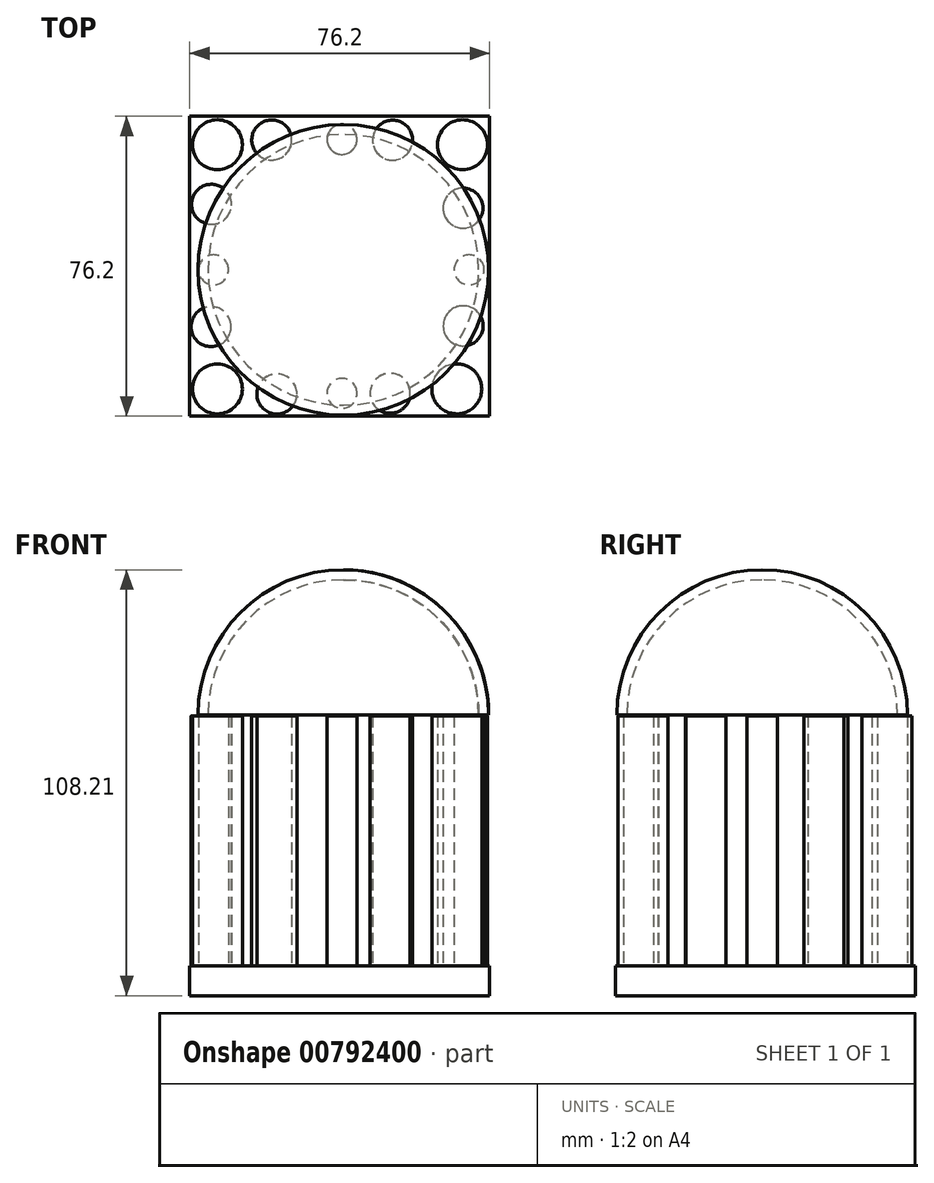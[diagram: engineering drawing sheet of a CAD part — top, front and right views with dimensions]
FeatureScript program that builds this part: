
annotation { "Feature Type Name" : "Feature", "Feature Type Description" : "" }
export const myFeature = defineFeature(function(context is Context, id is Id, definition is map)
    precondition{}
    {
        {
            var Q0;
            Q0=qCreatedBy(makeId("Top.planeOp"),FACE);
            var sketch = newSketch(context, id + "F0", { "sketchPlane" : qUnion([Q0])});
            skLineSegment(sketch, "E0.bottom", {"start": v(-38.66, 38.98) * mm, "end": v(37.54, 38.98) * mm});
            skLineSegment(sketch, "E0.top", {"start": v(-38.66, -37.22) * mm, "end": v(37.54, -37.22) * mm});
            skLineSegment(sketch, "E0.left", {"start": v(-38.66, 38.98) * mm, "end": v(-38.66, -37.22) * mm});
            skLineSegment(sketch, "E0.right", {"start": v(37.54, 38.98) * mm, "end": v(37.54, -37.22) * mm});
            skSolve(sketch);
        }
        {
            var Q0;
            Q0=makeQuery(id+"F0.imprint","IMPRINT",FACE,{"disambiguationData":[TD([[makeQuery(id+"F0.imprint","IMPRINT",EDGE,{"derivedFrom":sQuery(id+"F0.wireOp",EDGE,"E0.bottom")}),-1.0]])]});
            extrude(context, id + "F1", {"entities" : qUnion([Q0]), "depth" : 7.62 * mm, "offsetDistance" : 25.4 * mm});
        }
        {
            var Q0;
            Q0=makeQuery(id+"F1.opExtrude","CAP_FACE",FACE,{"disambiguationData":[OSD([sQuery(id+"F0.wireOp",EDGE,"E0.bottom"),sQuery(id+"F0.wireOp",EDGE,"E0.top"),sQuery(id+"F0.wireOp",EDGE,"E0.left"),sQuery(id+"F0.wireOp",EDGE,"E0.right")])],"isStart":false});
            var sketch = newSketch(context, id + "F2", { "sketchPlane" : qUnion([Q0])});
            skCircle(sketch, "E1", {"center": v(-31.66, -30.26) * mm, "radius": 6.35 * mm});
            skCircle(sketch, "E2", {"center": v(-31.66, 31.75) * mm, "radius": 6.35 * mm});
            skCircle(sketch, "E3", {"center": v(30.63, 31.75) * mm, "radius": 6.35 * mm});
            skCircle(sketch, "E4", {"center": v(29.17, -30.26) * mm, "radius": 6.35 * mm});
            skSolve(sketch);
        }
        {
            var Q0;
            Q0 = qSketchRegion(id + "F2", true);
            extrude(context, id + "F3", {"entities" : qUnion([Q0]), "operationType" : NewBodyOperationType.ADD, "depth" : 63.5 * mm, "offsetDistance" : 25.4 * mm});
        }
        {
            var Q0;
            Q0=makeQuery(id+"F1.opExtrude","CAP_FACE",FACE,{"disambiguationData":[OSD([sQuery(id+"F0.wireOp",EDGE,"E0.bottom"),sQuery(id+"F0.wireOp",EDGE,"E0.top"),sQuery(id+"F0.wireOp",EDGE,"E0.left"),sQuery(id+"F0.wireOp",EDGE,"E0.right")])],"isStart":false});
            var sketch = newSketch(context, id + "F4", { "sketchPlane" : qUnion([Q0])});
            skCircle(sketch, "E5", {"center": v(-32.63, 0) * mm, "radius": 3.81 * mm});
            skCircle(sketch, "E6", {"center": v(0, 33.12) * mm, "radius": 3.81 * mm});
            skCircle(sketch, "E7", {"center": v(32.3, 0) * mm, "radius": 3.81 * mm});
            skCircle(sketch, "E8", {"center": v(0, -31.4) * mm, "radius": 3.81 * mm});
            skCircle(sketch, "E9", {"center": v(-16.53, -31.56) * mm, "radius": 5.08 * mm});
            skCircle(sketch, "E10", {"center": v(12.25, -31.38) * mm, "radius": 5.08 * mm});
            skCircle(sketch, "E11", {"center": v(30.8, -14.26) * mm, "radius": 5.08 * mm});
            skCircle(sketch, "E12", {"center": v(30.75, 15.67) * mm, "radius": 5.08 * mm});
            skCircle(sketch, "E13", {"center": v(12.88, 32.92) * mm, "radius": 5.08 * mm});
            skCircle(sketch, "E14", {"center": v(-17.84, 32.96) * mm, "radius": 5.08 * mm});
            skCircle(sketch, "E15", {"center": v(-33.15, 16.64) * mm, "radius": 5.08 * mm});
            skCircle(sketch, "E16", {"center": v(-33.24, -14.45) * mm, "radius": 5.08 * mm});
            skSolve(sketch);
        }
        {
            var Q0;
            Q0 = qSketchRegion(id + "F4", true);
            extrude(context, id + "F5", {"entities" : qUnion([Q0]), "operationType" : NewBodyOperationType.ADD, "depth" : 63.5 * mm, "offsetDistance" : 25.4 * mm});
        }
        {
            var Q0;
            Q0=qCreatedBy(makeId("Front.planeOp"),FACE);
            var sketch = newSketch(context, id + "F6", { "sketchPlane" : qUnion([Q0])});
            skLineSegment(sketch, "E17", {"start": v(37.27, 71.3) * mm, "end": v(37.27, 71.3) * mm});
            skLineSegment(sketch, "E18", {"start": v(37.27, 71.3) * mm, "end": v(-36.57, 71.3) * mm});
            skArc(sketch, "E19", {"start": v(37.27, 71.3) * mm, "mid": v(0.35, 108.21) * mm, "end": v(-36.57, 71.3) * mm});
            skLineSegment(sketch, "E20", {"start": v(0.35, 71.3) * mm, "end": v(0.35, 108.21) * mm});
            skSolve(sketch);
        }
        {
            var Q0;
            {var subQ3=sQuery(id+"F6.wireOp",EDGE,"E20");Q0=makeQuery(id+"F6.imprint","IMPRINT",FACE,{"disambiguationData":[TD([[makeQuery(id+"F6.imprint","IMPRINT",EDGE,{"derivedFrom":subQ3}),-1.0]])]});}
            var Q1;
            Q1=sQuery(id+"F6.wireOp",EDGE,"E20");
            revolve(context, id + "F7", {"surfaceOperationType" : NewSurfaceOperationType.NEW, "entities" : qUnion([Q0]), "axis" : qUnion([Q1]), "revolveType" : RevolveType.FULL});
        }
        {
            var Q0;
            Q0=makeQuery(id+"F7.opRevolve","SWEPT_FACE",FACE,{"disambiguationData":[OSD([sQuery(id+"F6.wireOp",EDGE,"E18")])]});
            shell(context, id + "F8", {"entities" : qUnion([Q0]), "thickness" : 2.54 * mm});
        }
    });
